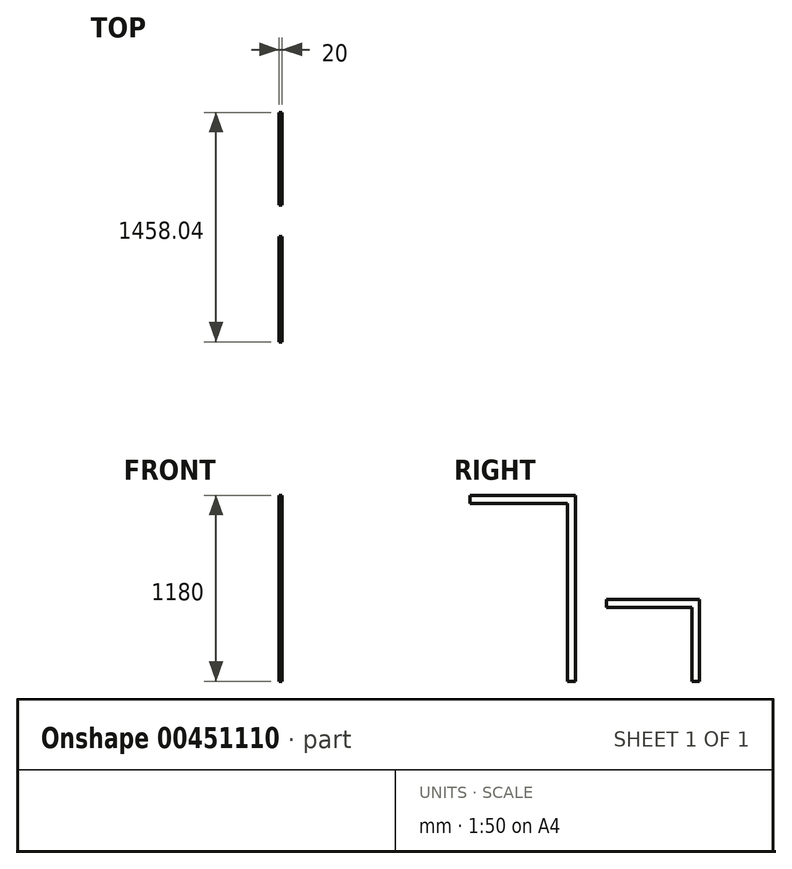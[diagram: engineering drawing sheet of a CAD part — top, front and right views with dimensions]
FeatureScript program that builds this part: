
annotation { "Feature Type Name" : "Feature", "Feature Type Description" : "" }
export const myFeature = defineFeature(function(context is Context, id is Id, definition is map)
    precondition{}
    {
        {
            var Q0;
            Q0=qCreatedBy(makeId("Right.planeOp"),FACE);
            var sketch = newSketch(context, id + "F0", { "sketchPlane" : qUnion([Q0])});
            skLineSegment(sketch, "E0", {"start": v(0, 0) * mm, "end": v(0, 470) * mm});
            skLineSegment(sketch, "E1", {"start": v(0, 470) * mm, "end": v(-540, 470) * mm});
            skLineSegment(sketch, "E2", {"start": v(-540, 470) * mm, "end": v(-540, 520) * mm});
            skLineSegment(sketch, "E3", {"start": v(-540, 520) * mm, "end": v(50, 520) * mm});
            skLineSegment(sketch, "E4", {"start": v(50, 520) * mm, "end": v(50, 0) * mm});
            skLineSegment(sketch, "E5", {"start": v(50, 0) * mm, "end": v(0, 0) * mm});
            skSolve(sketch);
        }
        {
            var Q0;
            Q0 = qSketchRegion(id + "F0", true);
            extrude(context, id + "F1", {"entities" : qUnion([Q0]), "depth" : 20 * mm, "offsetDistance" : 25 * mm});
        }
        {
            var Q0;
            Q0=qCreatedBy(makeId("Right.planeOp"),FACE);
            var sketch = newSketch(context, id + "F2", { "sketchPlane" : qUnion([Q0])});
            skLineSegment(sketch, "E6", {"start": v(-738.04, 0) * mm, "end": v(-738.04, 1180) * mm});
            skLineSegment(sketch, "E7", {"start": v(-738.04, 1180) * mm, "end": v(-1408.04, 1180) * mm});
            skLineSegment(sketch, "E8", {"start": v(-1408.04, 1180) * mm, "end": v(-1408.04, 1130) * mm});
            skLineSegment(sketch, "E9", {"start": v(-1408.04, 1130) * mm, "end": v(-788.04, 1130) * mm});
            skLineSegment(sketch, "E10", {"start": v(-788.04, 1130) * mm, "end": v(-788.04, 0) * mm});
            skLineSegment(sketch, "E11", {"start": v(-788.04, 0) * mm, "end": v(-738.04, 0) * mm});
            skSolve(sketch);
        }
        {
            var Q0;
            Q0 = qSketchRegion(id + "F2", true);
            extrude(context, id + "F3", {"entities" : qUnion([Q0]), "depth" : 20 * mm, "offsetDistance" : 25 * mm});
        }
    });
